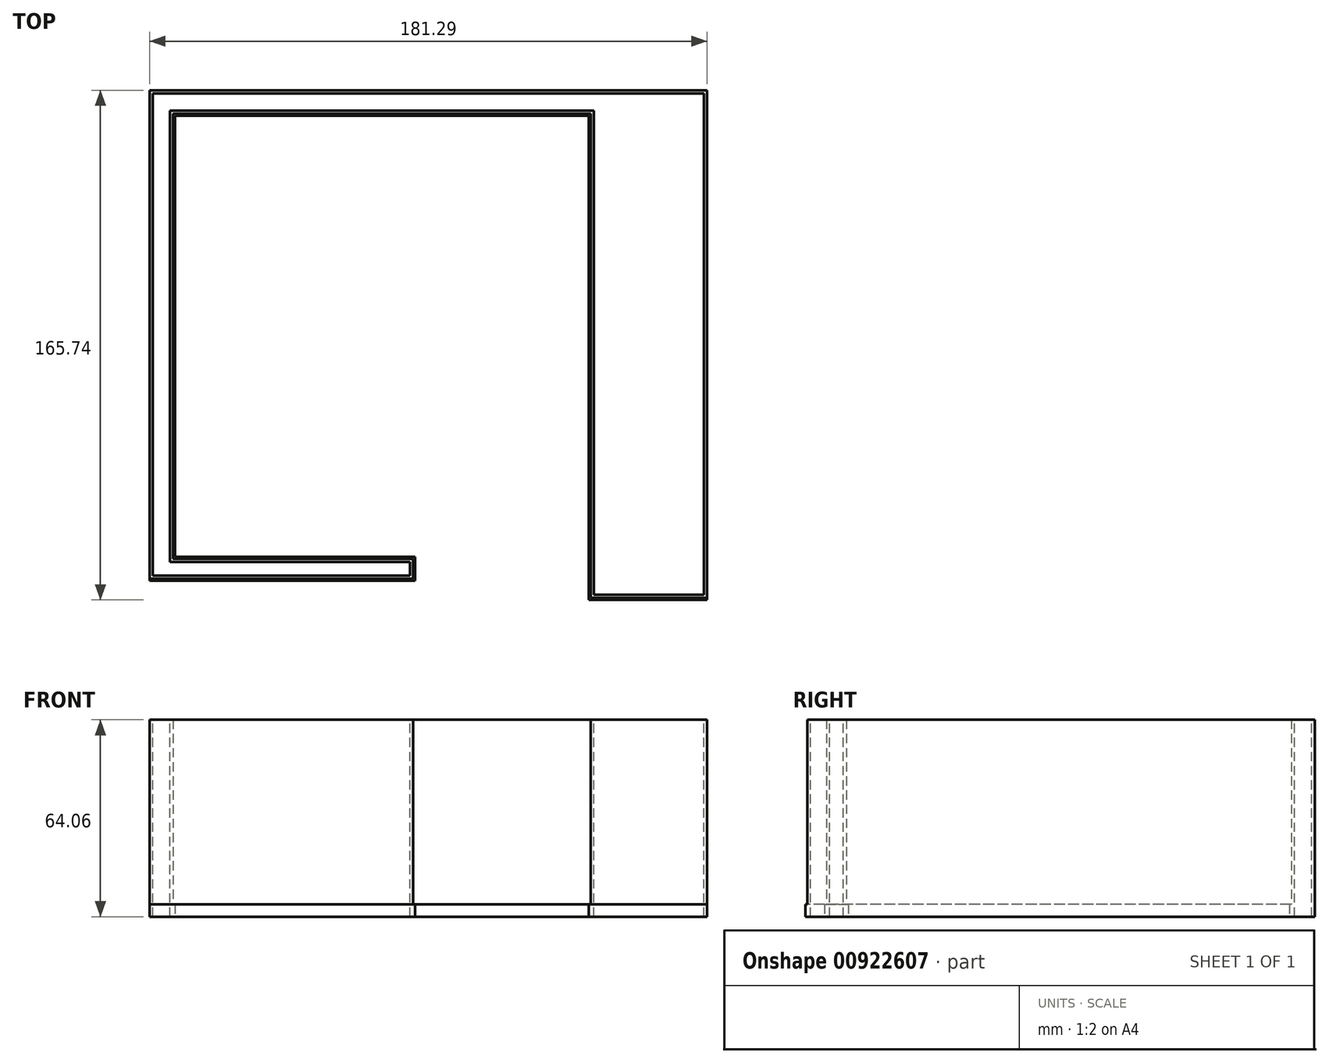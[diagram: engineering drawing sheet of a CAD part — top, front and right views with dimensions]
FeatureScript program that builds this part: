
annotation { "Feature Type Name" : "Feature", "Feature Type Description" : "" }
export const myFeature = defineFeature(function(context is Context, id is Id, definition is map)
    precondition{}
    {
        {
            assignVariable(context, id + "F0", {"name" : "f", "anyValue" : 0.1});
        }
        {
            var Q0;
            Q0=qCreatedBy(makeId("Top.planeOp"),FACE);
            var sketch = newSketch(context, id + "F1", { "sketchPlane" : qUnion([Q0])});
            skLineSegment(sketch, "E0", {"start": v(-1358.9, 1574.8) * mm, "end": v(1358.9, 1574.8) * mm});
            skLineSegment(sketch, "E1", {"start": v(1358.9, 1574.8) * mm, "end": v(1358.9, -1574.8) * mm});
            skLineSegment(sketch, "E2", {"start": v(-1358.9, 1574.8) * mm, "end": v(-1358.9, -1320.8) * mm});
            skLineSegment(sketch, "E3", {"start": v(-1358.9, 1574.8) * mm, "end": v(1358.9, -1574.8) * mm, "construction": true});
            skLineSegment(sketch, "E4", {"start": v(-1358.9, -1449.39) * mm, "end": v(203.2, -1449.39) * mm});
            skLineSegment(sketch, "E5", {"start": v(203.2, -1449.39) * mm, "end": v(203.2, -1320.8) * mm});
            skLineSegment(sketch, "E6", {"start": v(203.2, -1320.8) * mm, "end": v(-1358.9, -1320.8) * mm});
            skLineSegment(sketch, "E7", {"start": v(-1358.9, -1449.39) * mm, "end": v(-1511.3, -1449.39) * mm});
            skLineSegment(sketch, "E8", {"start": v(-1511.3, -1449.39) * mm, "end": v(-1511.3, 1727.2) * mm});
            skLineSegment(sketch, "E9", {"start": v(-1511.3, 1727.2) * mm, "end": v(2114.55, 1727.2) * mm});
            skLineSegment(sketch, "E10", {"start": v(2114.55, 1727.2) * mm, "end": v(2114.55, -1574.8) * mm});
            skLineSegment(sketch, "E11", {"start": v(2114.55, -1574.8) * mm, "end": v(1358.9, -1574.8) * mm});
            skSolve(sketch);
        }
        {
            var Q0;
            Q0 = qSketchRegion(id + "F1", true);
            extrude(context, id + "F2", {"entities" : qUnion([Q0]), "depth" : (6 * getVariable(context, 'f')) * mm, "offsetDistance" : 25.4 * mm});
        }
        {
            var Q0;
            Q0 = qSketchRegion(id + "F1", true);
            extrude(context, id + "F3", {"entities" : qUnion([Q0]), "operationType" : NewBodyOperationType.ADD, "depth" : 2562.22 * mm / 2, "offsetDistance" : 25.4 * mm});
        }
        {
            var Q0;
            Q0=qCreatedBy(makeId("Top.planeOp"),FACE);
            var sketch = newSketch(context, id + "F4", { "sketchPlane" : qUnion([Q0])});
            skLineSegment(sketch, "E12.0", {"start": v(203.2, -1449.39) * mm, "end": v(-1511.3, -1449.39) * mm});
            skLineSegment(sketch, "E12.1", {"start": v(203.2, -1449.39) * mm, "end": v(203.2, -1320.8) * mm});
            skLineSegment(sketch, "E12.2", {"start": v(203.2, -1320.8) * mm, "end": v(-1358.9, -1320.8) * mm});
            skLineSegment(sketch, "E12.3", {"start": v(1358.9, 1574.8) * mm, "end": v(1358.9, -1574.8) * mm});
            skLineSegment(sketch, "E12.4", {"start": v(2114.55, -1574.8) * mm, "end": v(1358.9, -1574.8) * mm});
            skLineSegment(sketch, "E12.5", {"start": v(-1358.9, 1574.8) * mm, "end": v(-1358.9, -1320.8) * mm});
            skLineSegment(sketch, "E12.6", {"start": v(-1358.9, 1574.8) * mm, "end": v(1358.9, 1574.8) * mm});
            skLineSegment(sketch, "E13.0", {"start": v(215.9, -1462.09) * mm, "end": v(-1511.3, -1462.09) * mm});
            skLineSegment(sketch, "E13.1", {"start": v(215.9, -1462.09) * mm, "end": v(215.9, -1308.1) * mm});
            skLineSegment(sketch, "E13.2", {"start": v(215.9, -1308.1) * mm, "end": v(-1346.2, -1308.1) * mm});
            skLineSegment(sketch, "E13.3", {"start": v(2114.55, -1587.5) * mm, "end": v(1346.2, -1587.5) * mm});
            skLineSegment(sketch, "E13.4", {"start": v(1346.2, 1562.1) * mm, "end": v(1346.2, -1587.5) * mm});
            skLineSegment(sketch, "E13.5", {"start": v(-1346.2, 1562.1) * mm, "end": v(1346.2, 1562.1) * mm});
            skLineSegment(sketch, "E13.6", {"start": v(-1346.2, 1562.1) * mm, "end": v(-1346.2, -1308.1) * mm});
            skLineSegment(sketch, "E14", {"start": v(-1511.3, -1462.09) * mm, "end": v(-1511.3, -1449.39) * mm});
            skLineSegment(sketch, "E15", {"start": v(2114.55, -1574.8) * mm, "end": v(2114.55, -1587.5) * mm});
            skSolve(sketch);
        }
        {
            var Q0;
            Q0 = qSketchRegion(id + "F4", true);
            extrude(context, id + "F5", {"entities" : qUnion([Q0]), "operationType" : NewBodyOperationType.ADD, "depth" : 79.38 * mm, "offsetDistance" : 25.4 * mm});
        }
        {
            var Q0;
            Q0=makeQuery(id+"F2.opExtrude","SWEPT_BODY",BODY,{"disambiguationData":[OSD([sQuery(id+"F1.wireOp",EDGE,"E0"),sQuery(id+"F1.wireOp",EDGE,"E1"),sQuery(id+"F1.wireOp",EDGE,"E2"),sQuery(id+"F1.wireOp",EDGE,"E4"),sQuery(id+"F1.wireOp",EDGE,"E5"),sQuery(id+"F1.wireOp",EDGE,"E6"),sQuery(id+"F1.wireOp",EDGE,"E7"),sQuery(id+"F1.wireOp",EDGE,"E8"),sQuery(id+"F1.wireOp",EDGE,"E9"),sQuery(id+"F1.wireOp",EDGE,"E10"),sQuery(id+"F1.wireOp",EDGE,"E11")])]});
            var Q1;
            Q1=qCreatedBy(makeId("Origin.pointOp"),VERTEX);
            transform(context, id + "F6", {"entities" : qUnion([Q0]), "transformType" : TransformType.SCALE_UNIFORMLY, "scale" : 0.05, "scalePoint" : qUnion([Q1]), "makeCopy" : false});
        }
        {
            var Q0;
            Q0=makeQuery(id+"F3.opExtrude","CAP_FACE",FACE,{"disambiguationData":[OSD([sQuery(id+"F1.wireOp",EDGE,"E0"),sQuery(id+"F1.wireOp",EDGE,"E1"),sQuery(id+"F1.wireOp",EDGE,"E2"),sQuery(id+"F1.wireOp",EDGE,"E4"),sQuery(id+"F1.wireOp",EDGE,"E5"),sQuery(id+"F1.wireOp",EDGE,"E6"),sQuery(id+"F1.wireOp",EDGE,"E7"),sQuery(id+"F1.wireOp",EDGE,"E8"),sQuery(id+"F1.wireOp",EDGE,"E9"),sQuery(id+"F1.wireOp",EDGE,"E10"),sQuery(id+"F1.wireOp",EDGE,"E11")])],"isStart":false});
            var sketch = newSketch(context, id + "F7", { "sketchPlane" : qUnion([Q0])});
            skLineSegment(sketch, "E16.0", {"start": v(-75.56, -72.47) * mm, "end": v(-75.57, 86.36) * mm, "construction": true});
            skLineSegment(sketch, "E16.1", {"start": v(-67.95, 78.74) * mm, "end": v(-67.94, -66.04) * mm, "construction": true});
            skLineSegment(sketch, "E16.2", {"start": v(-67.95, 78.74) * mm, "end": v(67.94, 78.74) * mm, "construction": true});
            skLineSegment(sketch, "E16.3", {"start": v(-75.57, 86.36) * mm, "end": v(105.73, 86.36) * mm, "construction": true});
            skLineSegment(sketch, "E16.4", {"start": v(105.73, 86.36) * mm, "end": v(105.73, -78.74) * mm, "construction": true});
            skLineSegment(sketch, "E16.5", {"start": v(67.94, 78.74) * mm, "end": v(67.95, -78.74) * mm, "construction": true});
            skLineSegment(sketch, "E16.6", {"start": v(10.16, -72.47) * mm, "end": v(-75.57, -72.47) * mm, "construction": true});
            skLineSegment(sketch, "E16.7", {"start": v(10.16, -66.04) * mm, "end": v(-67.94, -66.04) * mm, "construction": true});
            skLineSegment(sketch, "E16.8", {"start": v(10.16, -72.47) * mm, "end": v(10.16, -66.04) * mm, "construction": true});
            skLineSegment(sketch, "E17.0", {"start": v(105.73, -78.74) * mm, "end": v(67.95, -78.74) * mm, "construction": true});
            skLineSegment(sketch, "E18.0", {"start": v(-68.95, 79.74) * mm, "end": v(68.94, 79.74) * mm});
            skLineSegment(sketch, "E18.1", {"start": v(68.94, 79.74) * mm, "end": v(68.95, -77.74) * mm});
            skLineSegment(sketch, "E18.2", {"start": v(-68.95, 79.74) * mm, "end": v(-68.94, -67.04) * mm});
            skLineSegment(sketch, "E18.3", {"start": v(104.73, -77.74) * mm, "end": v(68.95, -77.74) * mm});
            skLineSegment(sketch, "E18.4", {"start": v(104.73, 85.36) * mm, "end": v(104.73, -77.74) * mm});
            skLineSegment(sketch, "E18.5", {"start": v(-74.57, 85.36) * mm, "end": v(104.73, 85.36) * mm});
            skLineSegment(sketch, "E18.6", {"start": v(9.16, -67.04) * mm, "end": v(-68.94, -67.04) * mm});
            skLineSegment(sketch, "E18.7", {"start": v(9.16, -71.47) * mm, "end": v(9.16, -67.04) * mm});
            skLineSegment(sketch, "E18.8", {"start": v(9.16, -71.47) * mm, "end": v(-74.56, -71.47) * mm});
            skLineSegment(sketch, "E18.9", {"start": v(-74.56, -71.47) * mm, "end": v(-74.57, 85.36) * mm});
            skSolve(sketch);
        }
        {
            var Q0;
            Q0 = qSketchRegion(id + "F7", true);
            var Q1;
            Q1=sQuery(id+"F7.wireOp",EDGE,"E16.6");
            var Q2;
            Q2=sQuery(id+"F7.wireOp",EDGE,"E16.8");
            var Q3;
            Q3=sQuery(id+"F7.wireOp",EDGE,"E16.7");
            var Q4;
            Q4=sQuery(id+"F7.wireOp",EDGE,"E16.1");
            var Q5;
            Q5=sQuery(id+"F7.wireOp",EDGE,"E16.0");
            var Q6;
            Q6=sQuery(id+"F7.wireOp",EDGE,"E16.3");
            var Q7;
            Q7=sQuery(id+"F7.wireOp",EDGE,"E16.2");
            var Q8;
            Q8=sQuery(id+"F7.wireOp",EDGE,"E16.5");
            var Q9;
            Q9=sQuery(id+"F7.wireOp",EDGE,"E16.4");
            var Q10;
            Q10=sQuery(id+"F7.wireOp",EDGE,"E17.0");
            extrude(context, id + "F8", {"entities" : qUnion([Q0]), "operationType" : NewBodyOperationType.REMOVE, "surfaceEntities" : qUnion([Q1, Q2, Q3, Q4, Q5, Q6, Q7, Q8, Q9, Q10]), "endBound" : BoundingType.UP_TO_NEXT, "oppositeDirection" : true, "depth" : 25.4 * mm, "offsetDistance" : 25.4 * mm});
        }
    });
